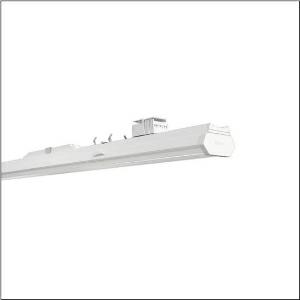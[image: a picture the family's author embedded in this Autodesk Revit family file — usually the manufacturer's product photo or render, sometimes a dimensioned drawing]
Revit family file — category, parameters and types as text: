
# Revit family: licross_r__11_protected_ho_51ts12vn4cxld_b83f
name_source: partatom
category: Lighting Fixtures
units: mm (PartAtom-declared; Revit-internal decimal feet)

## family parameters
Cut with Voids When Loaded = No
Host = Face
Light Source = No
Part Type = Normal
Room Calculation Point = No
Round Connector Dimension = Use Diameter
Shared = No

## types (1)
- --- (1 x LED, 1920 lm, 13.7 W, 4000K)
    Apparent Load = 14 VA
    CIE Flux Codes = 54 82 95 97 100
    Color Rendering = 80
    Color Temperature = 4000K
    Default Elevation = 1800 mm
    Description = Licross® 11 Protected HO, luminaire insert, of sheet steel, galvanised, coil coated, white, length: 1.500mm, width: 90mm, height: 101mm, LED rated luminous flux: 12.430lm, light colour: 840, control gear: DALI 2, CLO, control gear: ECG DALI, with plug, 6-pole, with phase selection, mains connection: 220..240V, AC/DC, 0/50..60Hz, halogen-free wiring, for central battery installations according to DIN EN 60598-2-22, for emergency light function, without changeover relay, luminous flux reduced to approx. 15% with DC operation, primary optical cover: cover, of PMMA, light emission: direct with ceiling illumination distribution, protection rating (complete): IP50, insulation class (complete): insulation class I (protective earthing), certification: CE, ENEC, VDE, UKCA, protection symbol: D if used in an environment with non-conductive dust loads with corresponding accessories, permissible ambient temperature for indoor applications: -25..+30°C, standard: EN 60598-2-22, corresponds to IFS (International Featured Standards) requirements for safety and quality in the food industry, reducing of maximum allowable ambient temperature of 5°C with ceiling mounting, packaging unit: 1 piece
    Height = 92 mm
    Lamp = 1 x LED
    Lamp Light Flux = 1920 lm
    Lamp Power = 13.7 W
    Lamp count = 1
    Length = 1500 mm
    Luminous efficacy = 140 lm/W
    Manufacturer = Siteco
    ModVariant = No
    Model = 51TS12VN4CXLD
    Mounting Place = Ceiling
    Mounting Type = Pendant
    Number of Poles = 1
    OnlyDefault = Yes
    Power Factor = 1
    Product Name = Licross® 11 Protected HO
    Product group = luminaire insert
    ProductGroupID = 902
    Protection Class = Protection class I
    Protection Degree = IP 50
    RLX_Detail_Level = 1
    RlxData = <blob elided: 24697 chars, md5=e71b7940>
    Socket = socket
    Standby Power = 0 W
    System Light Flux = 1920 lm
    System Power = 14 W
    Type Comments = : DC mode (central or group accumulator) initial emergency light level
    Type Image = l_1256145.jpg
    URL = http://relux.com
    VarID = @adj_128437
    Voltage = 0 V
    Weight = 0.00 kg
    Width = 88 mm

## geometry (parser evidence)
native form markers: Blend x4, Sweep x10
no freeform markers — native parametric forms only
